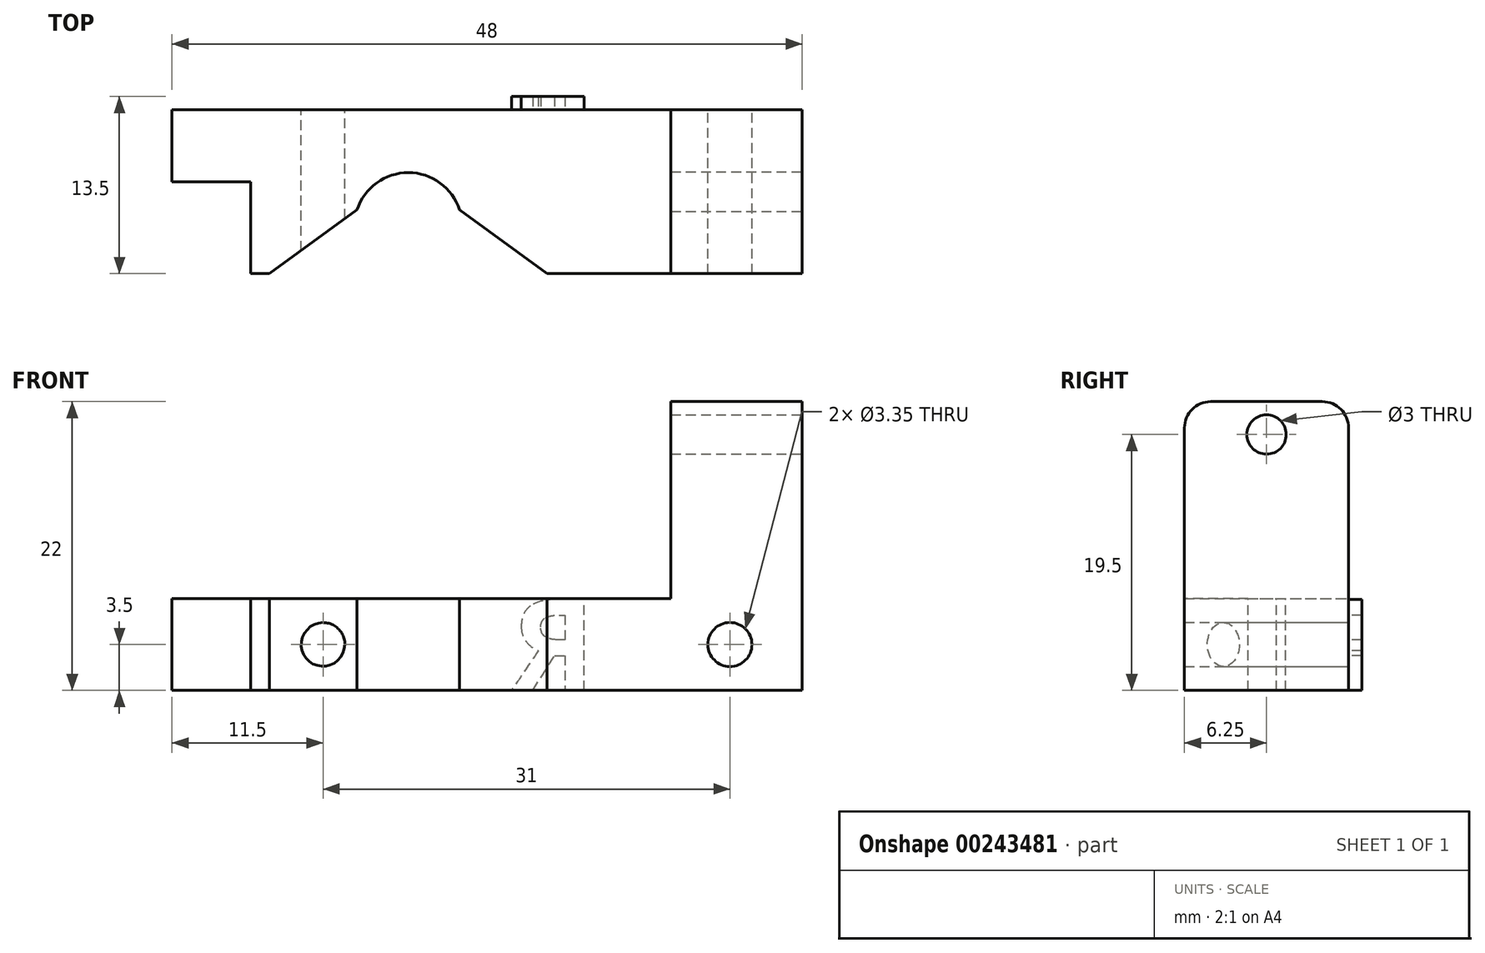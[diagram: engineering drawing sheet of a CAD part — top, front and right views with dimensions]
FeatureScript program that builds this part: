
annotation { "Feature Type Name" : "Feature", "Feature Type Description" : "" }
export const myFeature = defineFeature(function(context is Context, id is Id, definition is map)
    precondition{}
    {
        {
            assignVariable(context, id + "F0", {"name" : "rods", "anyValue" : 8});
        }
        {
            var Q0;
            Q0=qCreatedBy(makeId("Top.planeOp"),FACE);
            var sketch = newSketch(context, id + "F1", { "sketchPlane" : qUnion([Q0])});
            skLineSegment(sketch, "E0.bottom", {"start": v(0, 0) * mm, "end": v(42, 0) * mm});
            skLineSegment(sketch, "E0.top", {"start": v(0, 12.5) * mm, "end": v(42, 12.5) * mm});
            skLineSegment(sketch, "E0.left", {"start": v(0, 0) * mm, "end": v(0, 12.5) * mm});
            skLineSegment(sketch, "E0.right", {"start": v(42, 0) * mm, "end": v(42, 12.5) * mm});
            skSolve(sketch);
        }
        {
            var Q0;
            Q0=qSketchRegion(id+"F1",true);
            extrude(context, id + "F2", {"entities" : qUnion([Q0]), "depth" : 7 * mm});
        }
        {
            var Q0;
            Q0=makeQuery(id+"F2.opExtrude","CAP_FACE",FACE,{"disambiguationData":[OSD([sQuery(id+"F1.wireOp",EDGE,"E0.bottom"),sQuery(id+"F1.wireOp",EDGE,"E0.top"),sQuery(id+"F1.wireOp",EDGE,"E0.left"),sQuery(id+"F1.wireOp",EDGE,"E0.right")])],"isStart":false});
            var sketch = newSketch(context, id + "F3", { "sketchPlane" : qUnion([Q0])});
            skCircle(sketch, "E1", {"center": v(12, 3.6) * mm, "radius": 4.1 * mm});
            skSolve(sketch);
        }
        {
            var Q0;
            Q0=qSketchRegion(id+"F3",true);
            extrude(context, id + "F4", {"entities" : qUnion([Q0]), "operationType" : NewBodyOperationType.REMOVE, "oppositeDirection" : true, "depth" : 25 * mm});
        }
        {
            var Q0;
            Q0=makeQuery(id+"F4.boolean.opBoolean","INTERSECT",EDGE,{"disambiguationData":[OD(0.0)],"derivedFrom":[makeQuery(id+"F2.opExtrude","SWEPT_FACE",FACE,{"disambiguationData":[OSD([sQuery(id+"F1.wireOp",EDGE,"E0.bottom")])]}),makeQuery(id+"F4.opExtrude","SWEPT_FACE",FACE,{"disambiguationData":[OSD([sQuery(id+"F3.wireOp",EDGE,"E1")])]})]});
            var Q1;
            Q1=makeQuery(id+"F4.boolean.opBoolean","INTERSECT",EDGE,{"disambiguationData":[OD(1.0)],"derivedFrom":[makeQuery(id+"F2.opExtrude","SWEPT_FACE",FACE,{"disambiguationData":[OSD([sQuery(id+"F1.wireOp",EDGE,"E0.bottom")])]}),makeQuery(id+"F4.opExtrude","SWEPT_FACE",FACE,{"disambiguationData":[OSD([sQuery(id+"F3.wireOp",EDGE,"E1")])]})]});
            chamfer(context, id + "F5", {"entities" : qUnion([Q0, Q1]), "width" : (getVariable(context, 'rods') - 1) * mm, "tangentPropagation" : true});
        }
        {
            var Q0;
            Q0=makeQuery(id+"F2.opExtrude","SWEPT_FACE",FACE,{"disambiguationData":[OSD([sQuery(id+"F1.wireOp",EDGE,"E0.top")])]});
            var sketch = newSketch(context, id + "F6", { "sketchPlane" : qUnion([Q0])});
            skCircle(sketch, "E2", {"center": v(-5.5, 3.5) * mm, "radius": 1.68 * mm});
            skCircle(sketch, "E3", {"center": v(-36.5, 3.5) * mm, "radius": 1.68 * mm});
            skLineSegment(sketch, "E4", {"start": v(-5.5, 0) * mm, "end": v(-5.5, 7) * mm});
            skLineSegment(sketch, "E5", {"start": v(-5.5, 3.5) * mm, "end": v(0, 3.5) * mm});
            skLineSegment(sketch, "E6", {"start": v(-36.5, 3.5) * mm, "end": v(-42, 3.5) * mm});
            skSolve(sketch);
        }
        {
            var Q0;
            Q0=qSketchRegion(id+"F6",true);
            extrude(context, id + "F7", {"entities" : qUnion([Q0]), "operationType" : NewBodyOperationType.REMOVE, "oppositeDirection" : true, "depth" : 25 * mm});
        }
        {
            var Q0;
            Q0=makeQuery(id+"F2.opExtrude","SWEPT_FACE",FACE,{"disambiguationData":[OSD([sQuery(id+"F1.wireOp",EDGE,"E0.top")])]});
            var sketch = newSketch(context, id + "F8", { "sketchPlane" : qUnion([Q0])});
            skText(sketch, "E7", { "text": "R", "fontName": "OpenSans-Bold.ttf"});
            const initialGuessF8  = {"E7": [-0.02627, 0, 1, 0, 0.007]};
            skSetInitialGuess(sketch, initialGuessF8);
            skSolve(sketch);
        }
        {
            var Q0;
            Q0=qSketchRegion(id+"F8",true);
            extrude(context, id + "F9", {"entities" : qUnion([Q0]), "operationType" : NewBodyOperationType.ADD, "depth" : 1 * mm});
        }
        {
            var Q0;
            Q0=makeQuery(id+"F2.opExtrude","CAP_FACE",FACE,{"disambiguationData":[OSD([sQuery(id+"F1.wireOp",EDGE,"E0.bottom"),sQuery(id+"F1.wireOp",EDGE,"E0.top"),sQuery(id+"F1.wireOp",EDGE,"E0.left"),sQuery(id+"F1.wireOp",EDGE,"E0.right")])],"isStart":false});
            var sketch = newSketch(context, id + "F10", { "sketchPlane" : qUnion([Q0])});
            skLineSegment(sketch, "E8.bottom", {"start": v(42, 0) * mm, "end": v(32, 0) * mm});
            skLineSegment(sketch, "E8.top", {"start": v(42, 12.5) * mm, "end": v(32, 12.5) * mm});
            skLineSegment(sketch, "E8.left", {"start": v(42, 0) * mm, "end": v(42, 12.5) * mm});
            skLineSegment(sketch, "E8.right", {"start": v(32, 0) * mm, "end": v(32, 12.5) * mm});
            skSolve(sketch);
        }
        {
            var Q0;
            Q0=qSketchRegion(id+"F10",true);
            extrude(context, id + "F11", {"entities" : qUnion([Q0]), "operationType" : NewBodyOperationType.ADD, "depth" : 15 * mm});
        }
        {
            var Q0;
            Q0=makeQuery(id+"FJdLS7F1L1csLPb_1.boolean.opBoolean","MERGE",FACE,{"derivedFrom":[makeQuery(id+"F11.boolean.opBoolean","MERGE",FACE,{"derivedFrom":[makeQuery(id+"F2.opExtrude","SWEPT_FACE",FACE,{"disambiguationData":[OSD([sQuery(id+"F1.wireOp",EDGE,"E0.right")])]}),makeQuery(id+"F11.opExtrude","SWEPT_FACE",FACE,{"disambiguationData":[OSD([sQuery(id+"F10.wireOp",EDGE,"E8.left")])]})]}),makeQuery(id+"FJdLS7F1L1csLPb_1.opExtrude","SWEPT_FACE",FACE,{"disambiguationData":[OSD([sQuery(id+"F4Ds6MLMi3WL0gL_1.wireOp",EDGE,"f6963c6d-1d98-4eef-b5cd-deae189cd3ae.left")])]})]});
            var sketch = newSketch(context, id + "F12", { "sketchPlane" : qUnion([Q0])});
            skCircle(sketch, "E9", {"center": v(6.25, 19.5) * mm, "radius": 1.5 * mm});
            skPoint(sketch, "E10", {"position": v(0, 19.5) * mm});
            skPoint(sketch, "E11", {"position": v(6.25, 0) * mm});
            skSolve(sketch);
        }
        {
            var Q0;
            Q0=qSketchRegion(id+"F12",true);
            extrude(context, id + "F13", {"entities" : qUnion([Q0]), "operationType" : NewBodyOperationType.REMOVE, "oppositeDirection" : true, "depth" : 25 * mm});
        }
        {
            var Q0;
            Q0=makeQuery(id+"F11.opExtrude","CAP_EDGE",EDGE,{"disambiguationData":[OSD([sQuery(id+"F10.wireOp",EDGE,"E8.bottom")])],"isStart":false});
            var Q1;
            Q1=makeQuery(id+"F11.opExtrude","CAP_EDGE",EDGE,{"disambiguationData":[OSD([sQuery(id+"F10.wireOp",EDGE,"E8.top")])],"isStart":false});
            fillet(context, id + "F14", {"entities" : qUnion([Q0, Q1]), "radius" : 2 * mm, "tangentPropagation" : true, "allowEdgeOverflow" : false});
        }
        {
            var Q0;
            Q0=makeQuery(id+"F2.opExtrude","SWEPT_FACE",FACE,{"disambiguationData":[OSD([sQuery(id+"F1.wireOp",EDGE,"E0.left")])]});
            var sketch = newSketch(context, id + "F15", { "sketchPlane" : qUnion([Q0])});
            skLineSegment(sketch, "E12.bottom", {"start": v(-12.5, 0) * mm, "end": v(-7, 0) * mm});
            skLineSegment(sketch, "E12.top", {"start": v(-12.5, 7) * mm, "end": v(-7, 7) * mm});
            skLineSegment(sketch, "E12.left", {"start": v(-12.5, 0) * mm, "end": v(-12.5, 7) * mm});
            skLineSegment(sketch, "E12.right", {"start": v(-7, 0) * mm, "end": v(-7, 7) * mm});
            skSolve(sketch);
        }
        {
            var Q0;
            Q0=makeQuery(id+"F15.imprint","IMPRINT",FACE,{"disambiguationData":[TD([[makeQuery(id+"F15.imprint","IMPRINT",EDGE,{"derivedFrom":sQuery(id+"F15.wireOp",EDGE,"E12.bottom")}),-1.0]])]});
            extrude(context, id + "F16", {"entities" : qUnion([Q0]), "operationType" : NewBodyOperationType.ADD, "depth" : 6 * mm, "offsetDistance" : 25 * mm});
        }
    });
